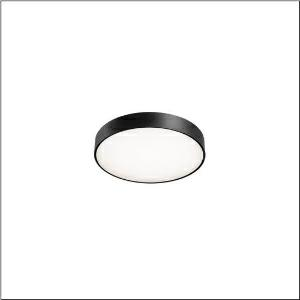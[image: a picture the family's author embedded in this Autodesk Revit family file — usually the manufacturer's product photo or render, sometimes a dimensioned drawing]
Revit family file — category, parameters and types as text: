
# Revit family: round_21_s_51mr34gd0321b
name_source: partatom
category: Lighting Fixtures
units: mm (PartAtom-declared; Revit-internal decimal feet)

## family parameters
Cut with Voids When Loaded = No
Host = Face
Light Source = No
Part Type = Normal
Room Calculation Point = No
Round Connector Dimension = Use Diameter
Shared = No

## types (1)
- Round 21 S (1 x LED, 3930 lm, 28.3 W, 3000K)
    Apparent Load = 28 VA
    CIE Flux Codes = 49 80 96 79 100
    Color Rendering = 80
    Color Temperature = 3000K
    Default Elevation = 1800 mm
    Description = Round 21 S, wall and ceiling luminaire, primary optical cover: cover, of PMMA, opal, light emission: direct/indirect distribution, primary light characteristic: symmetric, installation type: suspended mounting, surface-mounted, LED, rated luminous flux: 3.930lm, luminous efficacy: 139lm/W, light colour: 830, colour temperature: 3000K, control gear: DALI 2, with terminal, 5-pole, mains connection: 230V, AC, 50/60Hz, rated input power: 28.3W, housing, of aluminium, coated, black, diameter: 400mm, height: 62mm, protection rating (complete): IP40, insulation class (complete): insulation class I (protective earthing), certification: CE, impact resistance: IK04, permissible operating ambient temperature: -10..+35°C, packaging unit: 1 piece
    Height = 87 mm
    Lamp = 1 x LED
    Lamp Light Flux = 3930 lm
    Lamp Power = 28.3 W
    Lamp count = 1
    Length = 400 mm
    Luminous efficacy = 139 lm/W
    Manufacturer = Siteco
    ModVariant = No
    Model = 51MR34GD0321B
    Mounting Place = Wall
    Mounting Type = Surface mounted
    Number of Poles = 1
    OnlyDefault = Yes
    Power Factor = 1
    Product Name = Round 21 S
    Product group = wall and ceiling luminaire
    ProductGroupID = 2001
    Protection Class = Protection class I
    Protection Degree = IP 40
    RLX_Detail_Level = 1
    RLX_Emergency_Light_Flux = 0 lm
    RLX_Emergency_Type = 0
    RLX_Emergency_Type_DB = No
    RlxData = <blob elided: 13869 chars, md5=8bd4e101>
    Socket = socket
    Standby Power = 0 W
    System Light Flux = 3930 lm
    System Power = 28 W
    Type Comments = Product without accessories
    Type Image = l_1258311.jpg
    URL = http://relux.com
    VarID = ---
    Voltage = 0 V
    Weight = 0.00 kg
    Width = 0 mm  [stored 0 ft]

note: [stored X ft] marks values corroborated as IEEE doubles in the binary element streams (Revit-internal decimal feet)

## geometry (parser evidence)
native form markers: Sweep x12
no freeform markers — native parametric forms only
